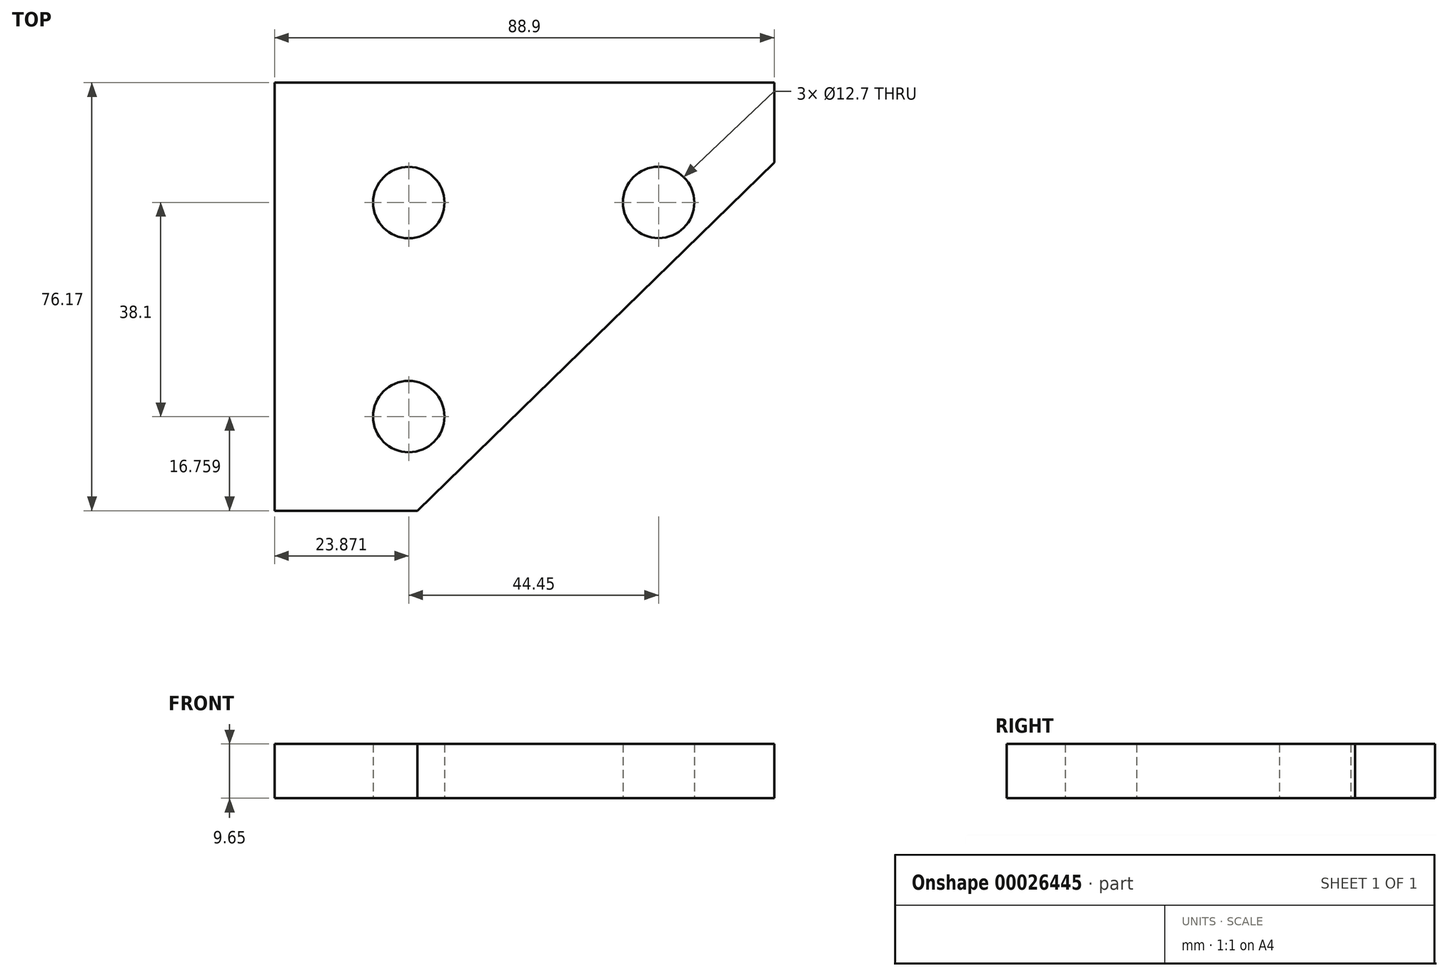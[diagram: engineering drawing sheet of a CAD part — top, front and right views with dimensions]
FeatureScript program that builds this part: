
annotation { "Feature Type Name" : "Feature", "Feature Type Description" : "" }
export const myFeature = defineFeature(function(context is Context, id is Id, definition is map)
    precondition{}
    {
        {
            var Q0;
            Q0=qCreatedBy(makeId("Top.planeOp"),FACE);
            var sketch = newSketch(context, id + "F0", { "sketchPlane" : qUnion([Q0])});
            skLineSegment(sketch, "E0.bottom", {"start": v(-42.72, 35.48) * mm, "end": v(46.18, 35.48) * mm});
            skLineSegment(sketch, "E0.top", {"start": v(-42.72, -40.7) * mm, "end": v(-17.3, -40.7) * mm});
            skLineSegment(sketch, "E0.left", {"start": v(-42.72, 35.48) * mm, "end": v(-42.72, -40.7) * mm});
            skLineSegment(sketch, "E0.right", {"start": v(46.18, 35.48) * mm, "end": v(46.18, 21.26) * mm});
            skLineSegment(sketch, "E1", {"start": v(-17.3, -40.7) * mm, "end": v(46.18, 21.26) * mm});
            skLineSegment(sketch, "E2.0", {"start": v(-18.85, 14.17) * mm, "end": v(-18.85, 14.15) * mm});
            skCircle(sketch, "E3", {"center": v(-18.85, 14.15) * mm, "radius": 6.35 * mm});
            skCircle(sketch, "E4", {"center": v(-18.85, -23.93) * mm, "radius": 6.35 * mm});
            skCircle(sketch, "E5", {"center": v(25.6, 14.17) * mm, "radius": 6.35 * mm});
            skLineSegment(sketch, "E6.trimOffspring", {"start": v(-18.85, -40.7) * mm, "end": v(-18.85, -40.72) * mm});
            skSolve(sketch);
        }
        {
            var Q0;
            Q0=makeQuery(id+"F0.imprint","IMPRINT",FACE,{"disambiguationData":[TD([[makeQuery(id+"F0.imprint","IMPRINT",EDGE,{"derivedFrom":sQuery(id+"F0.wireOp",EDGE,"E0.bottom")}),-1.0]])]});
            extrude(context, id + "F1", {"entities" : qUnion([Q0]), "depth" : 9.65 * mm});
        }
    });
